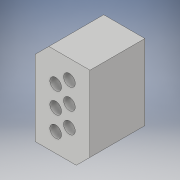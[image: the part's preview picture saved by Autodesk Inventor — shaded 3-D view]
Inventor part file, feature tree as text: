
AUTODESK INVENTOR PART (.ipt)
format: ipt  version: 2019 (Build 230136000, 136)  size: 204,800 bytes
history: native  units: mm
features: extrude x2, sketch x2, chamfer x1
ambient origin geometry x8: Origin, YZ Plane, XZ Plane, XY Plane, X Axis, Y Axis, Z Axis, Center Point
bodies: Volumenkörper1 (feature_tree)
feature tree (5):
  extrude  "Extrusion1"  Depth=2.0mm
  chamfer  "Fase1"  Distance=3.0mm
  extrude  "Extrusion2"  Depth=13.0mm
  sketch  "Skizze1"  dims[d0=1.7mm d1=2.0mm]
  sketch  "Skizze2"  dims[d2=1.5mm d3=3.0mm d4=1.7mm d5=1.7mm d6=1.7mm d7=1.7mm d8=1.7mm d9=3.0mm d10=3.0mm d11=3.0mm d16=8.0mm d17=0.0mm d18=2.0mm d19=2.0mm d20=45.0deg d21=0.1mm d22=0.0mm d23=8.0mm d24=2.0mm d25=3.0mm d26=13.0mm d27=7.5mm d28=2.75mm]
